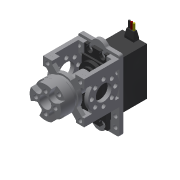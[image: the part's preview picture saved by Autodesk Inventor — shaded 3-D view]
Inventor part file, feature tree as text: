
AUTODESK INVENTOR PART (.ipt)
format: ipt  version: 2013 (Build 170138000, 138)  size: 765,952 bytes
history: native  units: in
note: dims shown in document units (in); Inventor stores cm internally (conversion verified against a paired STEP export)
features: extrude x23, sketch x23, other x11, projected_geometry x10, fillet x3, mirror x2, plane x1, pattern_circular x1
ambient origin geometry x8: Origin, YZ Plane, XZ Plane, XY Plane, X Axis, Y Axis, Z Axis, Center Point
feature tree (74):
  other  "Servo"
  extrude  "Extrusion1"  Depth=1.525in
  extrude  "Extrusion2"  Depth=0.025in
  extrude  "Extrusion3"  Depth=0.17in
  fillet  "Fillet1"  Radius=0.11in
  plane  "Work Plane1"
  extrude  "Extrusion4"  Depth=0.391in
  fillet  "Fillet2"  Radius=0.07in
  mirror  "Mirror1"
  extrude  "Extrusion5"  [1 undecoded]
  extrude  "Extrusion6"  Depth=0.28in
  extrude  "Extrusion7"  Depth=0.165in
  extrude  "Extrusion8"  Depth=0.1in TaperAngle=0.0deg
  extrude  "Extrusion9"  Depth=0.3in
  extrude  "Extrusion10"  Depth=0.01in
  fillet  "Fillet3"  Radius=0.0625in
  extrude  "Extrusion11"  Depth=0.0625in
  extrude  "Extrusion12"  Depth=0.0625in
  extrude  "Extrusion13"  Depth=0.2in TaperAngle=0.0deg
  extrude  "Extrusion14"  Depth=0.04in
  extrude  "Extrusion15"  Depth=0.136in
  extrude  "Extrusion16"  Depth=0.125in
  mirror  "Mirror2"
  extrude  "Extrusion18"  Depth=0.25in
  extrude  "Extrusion19"  Depth=0.2165in
  extrude  "Extrusion20"  Depth=0.1325in
  extrude  "Extrusion21"  Depth=0.3125in
  extrude  "Extrusion22"  Depth=0.125in TaperAngle=0.0deg
  extrude  "Extrusion23"  Depth=0.125in
  extrude  "Extrusion24"  Depth=0.083in
  pattern_circular  "Circular Pattern1"  [2 undecoded]
  sketch  "Sketch1"  dims[d0=0.782in d1=1.525in]
  sketch  "Sketch2"  dims[d2=1.305in d3=0.0in d4=0.025in]
  sketch  "Sketch3"  dims[d5=0.025in d6=0.17in d7=0.11in d8=0.0in]
  sketch  "Sketch4"  dims[d9=0.508in d11=0.391in d12=0.07in d13=0.0in]
  sketch  "Sketch5"  dims[d14=0.366in d15=-0.16in]
  sketch  "Sketch6"  dims[d16=0.737in d18=0.28in]
  sketch  "Sketch7"  dims[d19=0.1in d20=0.21in d21=0.165in]
  other  "Red wire"
  sketch  "Sketch8"  dims[d22=0.165in d23=0.1in d24=0.0in]
  sketch  "Sketch9"  dims[d25=0.01in d26=0.3in]
  other  "Yellow Wire"
  sketch  "Sketch10"  dims[d27=0.17in d28=0.01in d29=0.0625in d30=0.0in]
  other  "BaseStructure"
  sketch  "Sketch11"  dims[d31=0.2in d32=-0.0687in d33=0.0625in]
  other  "ServoOutput"
  sketch  "Sketch12"  dims[d34=0.2in d35=0.0in d36=0.0625in]
  other  "SideStructure"
  sketch  "Sketch13"  dims[d37=0.04in d38=0.2in d39=0.0in]
  sketch  "Sketch14"  dims[d40=0.0625in d41=0.04in]
  projected_geometry  "Projected Loop1"
  projected_geometry  "Projected Loop2"
  sketch  "Sketch16"  dims[d42=0.2in d43=0.0in d44=0.136in]
  sketch  "Sketch17"  dims[d47=2.25in d48=0.125in]
  other  "Pattern of SideStructure:1"
  other  "SideStructureMirror"
  sketch  "Sketch18"  dims[d49=0.25in d50=0.25in]
  projected_geometry  "Projected Loop3"
  projected_geometry  "Projected Loop4"
  projected_geometry  "Projected Loop5"
  projected_geometry  "Projected Loop6"
  projected_geometry  "Projected Loop7"
  other  "BearingStructure"
  sketch  "Sketch19"  dims[d51=0.125in d52=0.2165in]
  sketch  "Sketch20"  dims[d53=0.1325in d54=0.1325in]
  other  "HubShaft"
  sketch  "Sketch21"  dims[d55=1.3125in d56=0.3125in]
  sketch  "Sketch22"  dims[d57=0.435in d58=0.125in d59=0.0in]
  sketch  "Sketch23"  dims[d60=0.0625in d61=0.125in]
  other  "HubAdapter"
  sketch  "Sketch24"  dims[d62=0.0625in d63=0.0in d66=0.083in d67=0.083in d68=0.125in d69=0.125in d70=0.125in d71=0.0in d72=0.125in d73=0.75in d74=0.0in d75=0.125in d76=0.0in d80=1.0in d82=0.125in d83=0.0in d84=0.5in d85=0.75in d86=0.136in d87=3.1496in d89=360.0deg d91=0.125in d92=0.0in d93=0.95in d94=45.0deg d96=0.26in d97=0.13in d100=45.0deg d101=0.13in d102=0.26in d103=0.125in d104=0.0in d105=0.845in d106=0.072in d107=0.0in d108=0.5in d109=0.8575in d110=0.0in d111=1.0in d112=0.75in d113=0.136in d114=3.1496in d116=360.0deg d118=0.2in d119=0.0in d120=0.3in d121=0.2in d122=0.0in d123=0.375in d124=0.625in d125=0.136in d126=1.5748in d128=360.0deg d130=0.25in d131=0.0in d133=0.1374in d134=0.1374in d135=0.168in d136=0.0in d137=1.5748in d138=360.0deg]
  projected_geometry  "Project Cut Edges1"
  projected_geometry  "Project Cut Edges2"
  projected_geometry  "Project Cut Edges3"
note: 3 required parameter values undecoded (feature->parameter linkage not recoverable at this tier; creation-order binding heuristic only, values carry confidence <= 0.55)
